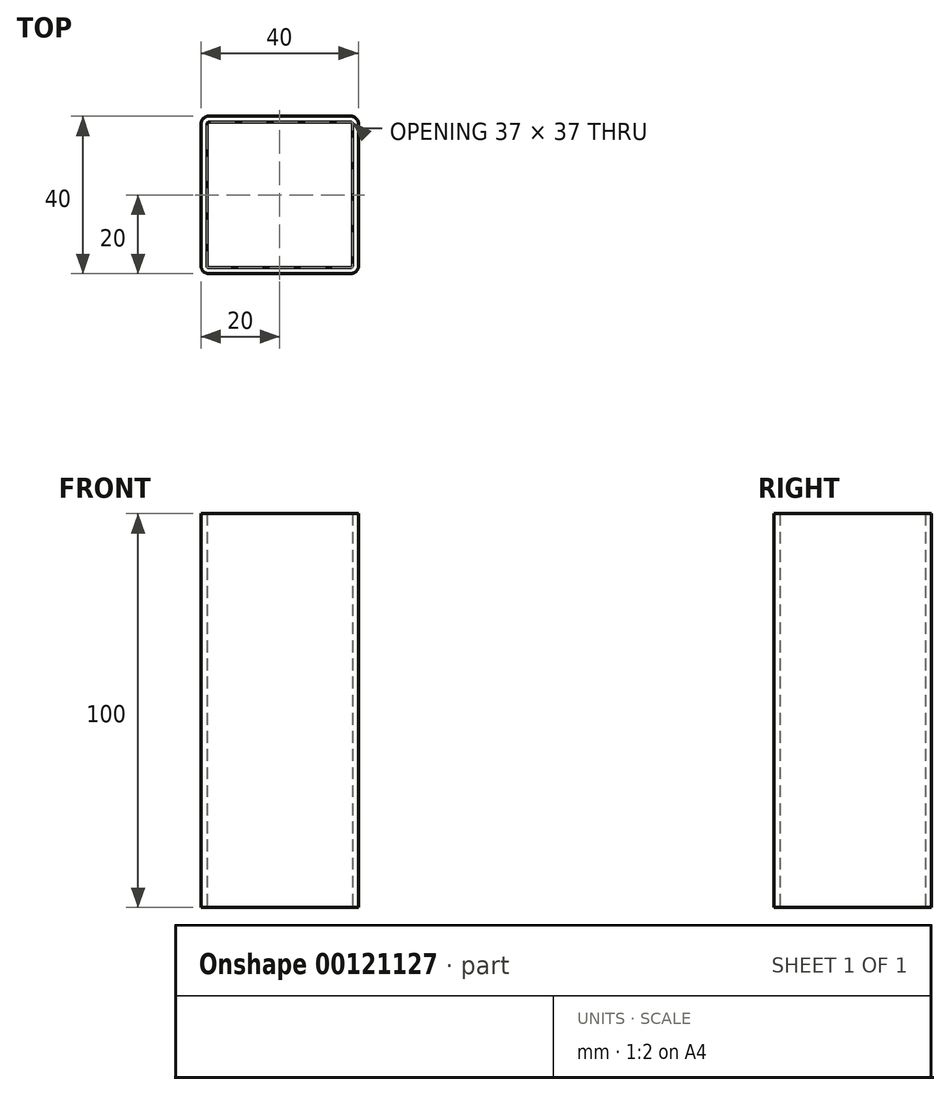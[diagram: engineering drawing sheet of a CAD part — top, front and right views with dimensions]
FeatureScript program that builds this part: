
annotation { "Feature Type Name" : "Feature", "Feature Type Description" : "" }
export const myFeature = defineFeature(function(context is Context, id is Id, definition is map)
    precondition{}
    {
        {
            var Q0;
            Q0=qCreatedBy(makeId("Top.planeOp"),FACE);
            var sketch = newSketch(context, id + "F0", { "sketchPlane" : qUnion([Q0])});
            skLineSegment(sketch, "E0.bottom", {"start": v(18, -20) * mm, "end": v(-18, -20) * mm});
            skLineSegment(sketch, "E0.top", {"start": v(18, 20) * mm, "end": v(-18, 20) * mm});
            skLineSegment(sketch, "E0.left", {"start": v(20, -18) * mm, "end": v(20, 18) * mm});
            skLineSegment(sketch, "E0.right", {"start": v(-20, -18) * mm, "end": v(-20, 18) * mm});
            skPoint(sketch, "E0.middle", {"position": v(0, 0) * mm});
            skPoint(sketch, "E1.visualSharp", {"position": v(-20, 20) * mm});
            skArc(sketch, "E1.filletArc", {"start": v(-18, 20) * mm, "mid": v(-19.41, 19.41) * mm, "end": v(-20, 18) * mm});
            skPoint(sketch, "E2.visualSharp", {"position": v(20, 20) * mm});
            skArc(sketch, "E2.filletArc", {"start": v(20, 18) * mm, "mid": v(19.41, 19.41) * mm, "end": v(18, 20) * mm});
            skPoint(sketch, "E3.visualSharp", {"position": v(20, -20) * mm});
            skArc(sketch, "E3.filletArc", {"start": v(18, -20) * mm, "mid": v(19.41, -19.41) * mm, "end": v(20, -18) * mm});
            skPoint(sketch, "E4.visualSharp", {"position": v(-20, -20) * mm});
            skArc(sketch, "E4.filletArc", {"start": v(-20, -18) * mm, "mid": v(-19.41, -19.41) * mm, "end": v(-18, -20) * mm});
            skPoint(sketch, "E5.visualSharp", {"position": v(-18.5, 18.5) * mm});
            skArc(sketch, "E6.0", {"start": v(18, -18.5) * mm, "mid": v(18.35, -18.35) * mm, "end": v(18.5, -18) * mm});
            skLineSegment(sketch, "E6.1", {"start": v(18.5, -18) * mm, "end": v(18.5, 18) * mm});
            skLineSegment(sketch, "E6.2", {"start": v(18, -18.5) * mm, "end": v(-18, -18.5) * mm});
            skArc(sketch, "E6.3", {"start": v(18.5, 18) * mm, "mid": v(18.35, 18.35) * mm, "end": v(18, 18.5) * mm});
            skArc(sketch, "E6.4", {"start": v(-18.5, -18) * mm, "mid": v(-18.35, -18.35) * mm, "end": v(-18, -18.5) * mm});
            skLineSegment(sketch, "E6.5", {"start": v(-18.5, -18) * mm, "end": v(-18.5, 18) * mm});
            skArc(sketch, "E6.6", {"start": v(-18, 18.5) * mm, "mid": v(-18.35, 18.35) * mm, "end": v(-18.5, 18) * mm});
            skLineSegment(sketch, "E6.7", {"start": v(18, 18.5) * mm, "end": v(-18, 18.5) * mm});
            skSolve(sketch);
        }
        {
            var Q0;
            Q0=makeQuery(id+"F0.imprint","IMPRINT",FACE,{"disambiguationData":[TD([[makeQuery(id+"F0.imprint","IMPRINT",EDGE,{"derivedFrom":sQuery(id+"F0.wireOp",EDGE,"E0.bottom")}),-1.0]])]});
            extrude(context, id + "F1", {"entities" : qUnion([Q0]), "depth" : 100 * mm});
        }
    });
